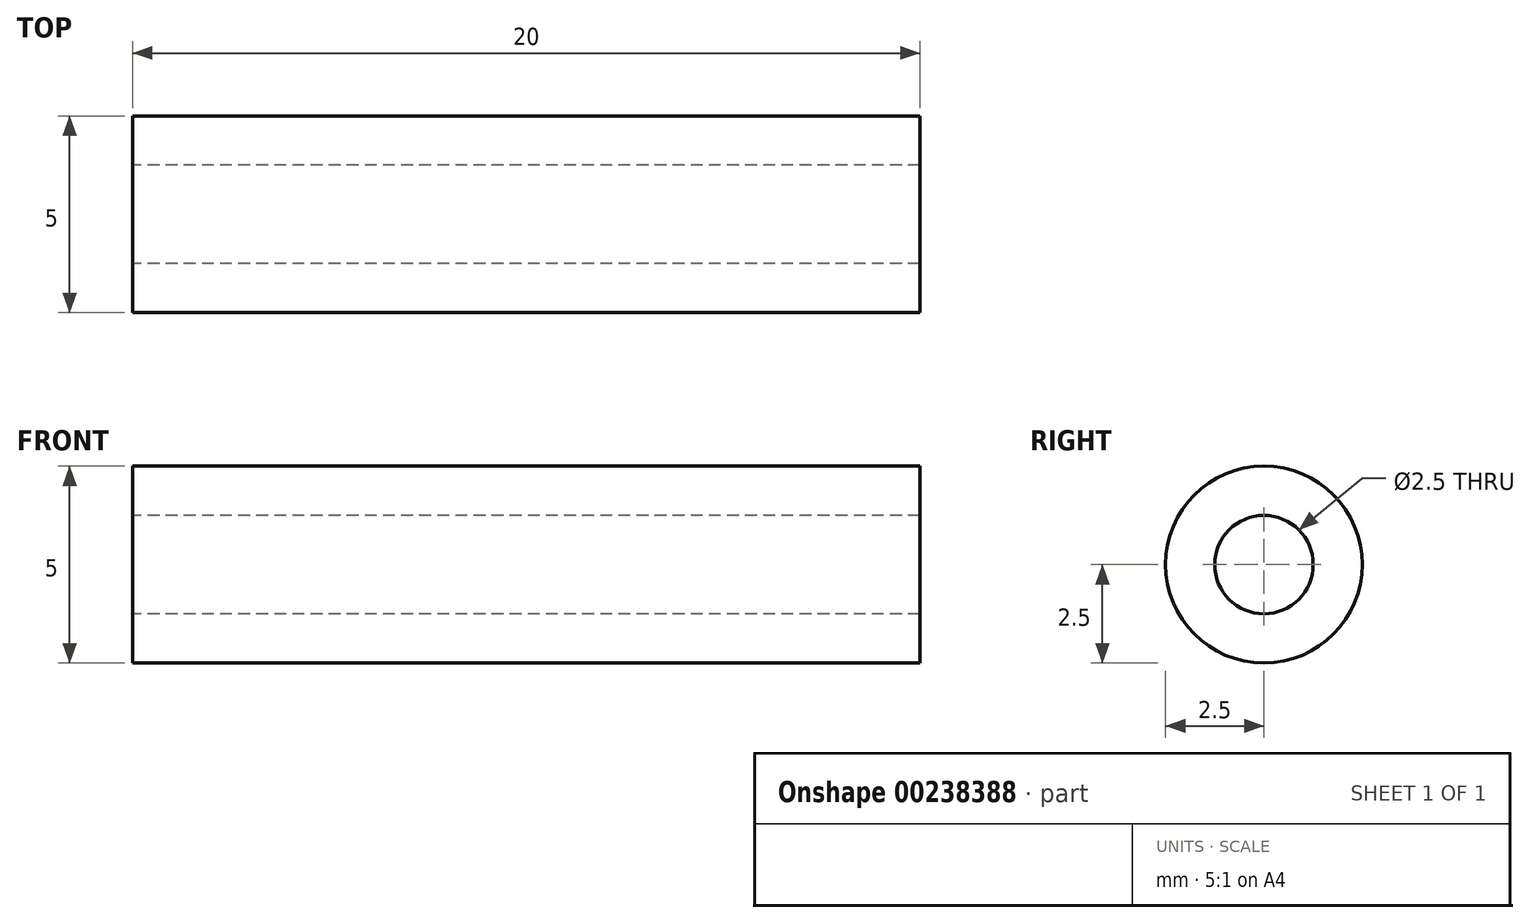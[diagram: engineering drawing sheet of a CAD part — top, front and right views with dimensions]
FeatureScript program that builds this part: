
annotation { "Feature Type Name" : "Feature", "Feature Type Description" : "" }
export const myFeature = defineFeature(function(context is Context, id is Id, definition is map)
    precondition{}
    {
        {
            var Q0;
            Q0=qCreatedBy(makeId("Right.planeOp"),FACE);
            var sketch = newSketch(context, id + "F0", { "sketchPlane" : qUnion([Q0])});
            skCircle(sketch, "E0", {"center": v(0, 0) * mm, "radius": 2.5 * mm});
            skCircle(sketch, "E1", {"center": v(0, 0) * mm, "radius": 1.25 * mm});
            skSolve(sketch);
        }
        {
            var Q0;
            Q0=makeQuery(id+"F0.imprint","IMPRINT",FACE,{"disambiguationData":[TD([[makeQuery(id+"F0.imprint","IMPRINT",EDGE,{"derivedFrom":sQuery(id+"F0.wireOp",EDGE,"E0")}),1.0]])]});
            extrude(context, id + "F1", {"entities" : qUnion([Q0]), "depth" : 20 * mm});
        }
    });
